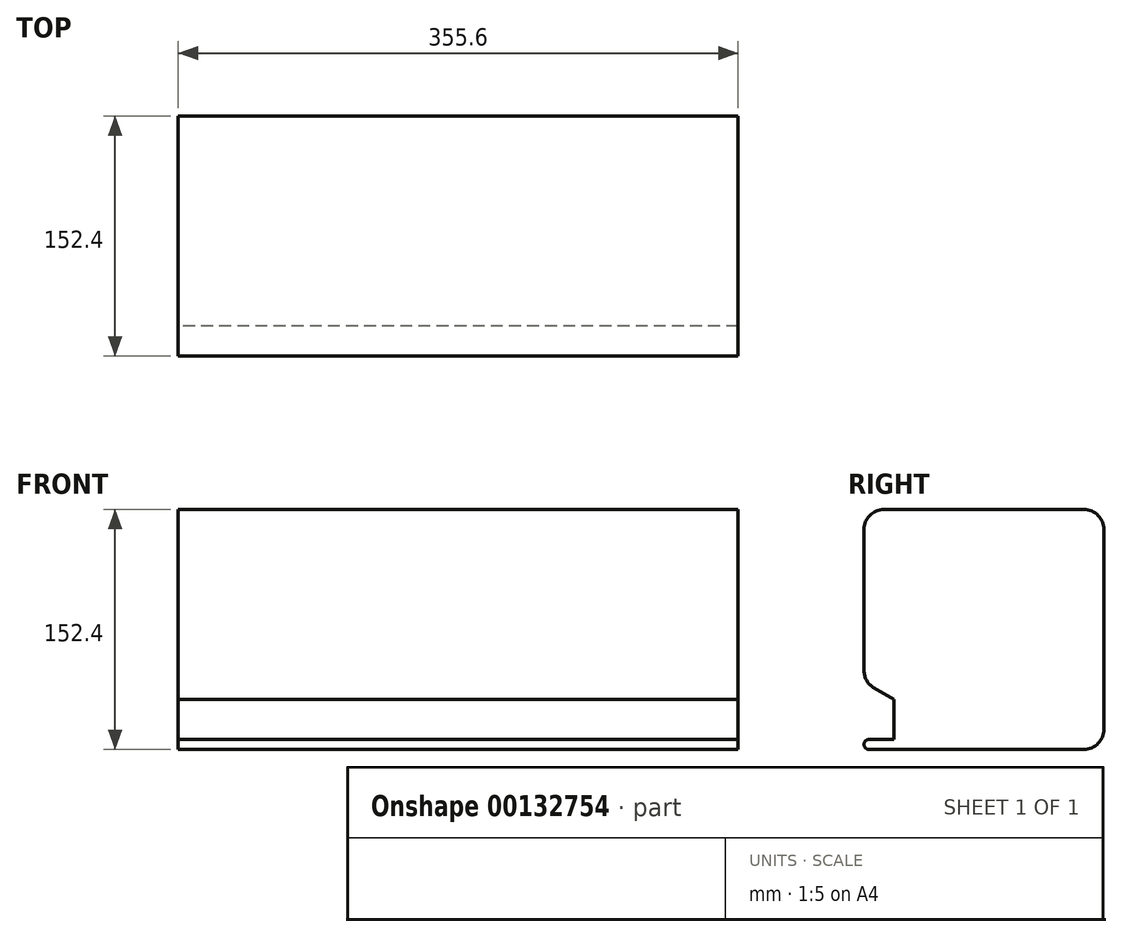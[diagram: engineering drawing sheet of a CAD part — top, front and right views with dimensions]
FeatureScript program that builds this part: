
annotation { "Feature Type Name" : "Feature", "Feature Type Description" : "" }
export const myFeature = defineFeature(function(context is Context, id is Id, definition is map)
    precondition{}
    {
        {
            var Q0;
            Q0=qCreatedBy(makeId("Right.planeOp"),FACE);
            var sketch = newSketch(context, id + "F0", { "sketchPlane" : qUnion([Q0])});
            skLineSegment(sketch, "E0.bottom", {"start": v(71, 71.31) * mm, "end": v(-81.4, 71.31) * mm});
            skLineSegment(sketch, "E0.top", {"start": v(71, -81.09) * mm, "end": v(-81.4, -81.09) * mm});
            skLineSegment(sketch, "E0.left", {"start": v(71, 71.31) * mm, "end": v(71, -81.09) * mm});
            skLineSegment(sketch, "E0.right", {"start": v(-81.4, 71.31) * mm, "end": v(-81.4, -38.34) * mm});
            skLineSegment(sketch, "E1", {"start": v(-81.4, -74.74) * mm, "end": v(-62.35, -74.74) * mm});
            skLineSegment(sketch, "E2", {"start": v(-62.35, -74.74) * mm, "end": v(-62.35, -49.34) * mm});
            skLineSegment(sketch, "E3", {"start": v(-62.35, -49.34) * mm, "end": v(-81.4, -38.34) * mm});
            skLineSegment(sketch, "E4.trimOffspring", {"start": v(-81.4, -74.74) * mm, "end": v(-81.4, -81.09) * mm});
            skSolve(sketch);
        }
        {
            var Q0;
            Q0=makeQuery(id+"F0.imprint","IMPRINT",FACE,{"disambiguationData":[TD([[makeQuery(id+"F0.imprint","IMPRINT",EDGE,{"derivedFrom":sQuery(id+"F0.wireOp",EDGE,"E0.bottom")}),1.0]])]});
            extrude(context, id + "F1", {"entities" : qUnion([Q0]), "endBound" : BoundingType.SYMMETRIC, "depth" : 355.6 * mm});
        }
        {
            var Q0;
            Q0=makeQuery(id+"F1.opExtrude","SWEPT_EDGE",EDGE,{"disambiguationData":[OSD([sQuery(id+"F0.wireOp",EDGE,"E0.right"),sQuery(id+"F0.wireOp",EDGE,"E3")])]});
            var Q1;
            Q1=makeQuery(id+"F1.opExtrude","SWEPT_EDGE",EDGE,{"disambiguationData":[OSD([sQuery(id+"F0.wireOp",EDGE,"E0.bottom"),sQuery(id+"F0.wireOp",EDGE,"E0.right")])]});
            var Q2;
            Q2=makeQuery(id+"F1.opExtrude","SWEPT_EDGE",EDGE,{"disambiguationData":[OSD([sQuery(id+"F0.wireOp",EDGE,"E0.bottom"),sQuery(id+"F0.wireOp",EDGE,"E0.left")])]});
            var Q3;
            Q3=makeQuery(id+"F1.opExtrude","SWEPT_EDGE",EDGE,{"disambiguationData":[OSD([sQuery(id+"F0.wireOp",EDGE,"E0.top"),sQuery(id+"F0.wireOp",EDGE,"E0.left")])]});
            fillet(context, id + "F2", {"entities" : qUnion([Q0, Q1, Q2, Q3]), "radius" : 12.7 * mm, "tangentPropagation" : true, "allowEdgeOverflow" : false});
        }
        {
            var Q0;
            Q0=makeQuery(id+"F1.opExtrude","SWEPT_EDGE",EDGE,{"disambiguationData":[OSD([sQuery(id+"F0.wireOp",EDGE,"E1"),sQuery(id+"F0.wireOp",EDGE,"E4.trimOffspring")])]});
            var Q1;
            Q1=makeQuery(id+"F1.opExtrude","SWEPT_EDGE",EDGE,{"disambiguationData":[OSD([sQuery(id+"F0.wireOp",EDGE,"E0.top"),sQuery(id+"F0.wireOp",EDGE,"E4.trimOffspring")])]});
            fillet(context, id + "F3", {"entities" : qUnion([Q0, Q1]), "radius" : 3.17 * mm, "tangentPropagation" : true, "allowEdgeOverflow" : false});
        }
    });
